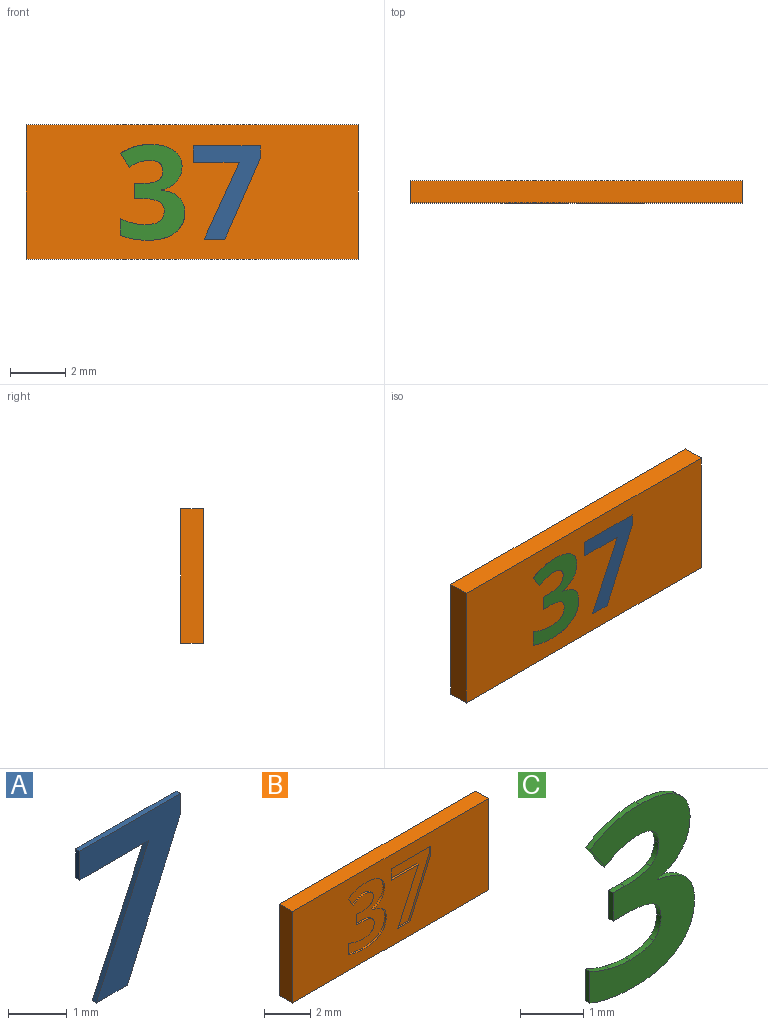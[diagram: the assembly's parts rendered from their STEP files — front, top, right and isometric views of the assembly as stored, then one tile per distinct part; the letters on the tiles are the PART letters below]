
ASSEMBLY  parts=3 mates=2
PART A: 9 faces, bbox 2.4x0.1x3.4 mm
  f0: plane 3.37x2.42mm, normal (0,-1,0), area 3.4mm2, adj f1,f2,f3,f4,f6,f7,f8
  f1: plane 2.92x1.28mm, normal (0.92,0,-0.4), area 0.3mm2, adj f0,f2,f5,f7
  f2: plane 0.45x0.1mm, normal (1,0,0), area 0mm2, adj f0,f1,f3,f5
  f3: plane 2.42x0.1mm, normal (0,0,1), area 0.2mm2, adj f0,f2,f4,f5
  f4: plane 0.6x0.1mm, normal (-1,0,0), area 0.1mm2, adj f0,f3,f5,f6
  f5: plane 3.37x2.42mm, normal (0,1,0), area 3.4mm2, adj f1,f2,f3,f4,f6,f7,f8
  f6: plane 1.66x0.1mm, normal (0,0,-1), area 0.2mm2, adj f0,f4,f5,f8
  f7: plane 0.75x0.1mm, normal (0,0,-1), area 0.1mm2, adj f0,f1,f5,f8
  f8: plane 2.77x1.27mm, normal (-0.91,0,0.42), area 0.3mm2, adj f0,f5,f6,f7
PART B: 42 faces, bbox 12x0.8x4.9 mm
  f0: plane 12x4.85mm, normal (0,-1,0), area 50.5mm2, adj f1,f2,f3,f4,f6,f7,f8,f9
  f1: plane 12x0.8mm, normal (0,0,-1), area 9.6mm2, adj f0,f2,f4,f5
  f2: plane 4.85x0.8mm, normal (1,0,0), area 3.9mm2, adj f0,f1,f3,f5
  f3: plane 12x0.8mm, normal (0,0,1), area 9.6mm2, adj f0,f2,f4,f5
  f4: plane 4.85x0.8mm, normal (-1,0,0), area 3.9mm2, adj f0,f1,f3,f5
  f5: plane 12x4.85mm, normal (0,1,0), area 58.2mm2, adj f1,f2,f3,f4
  f6: plane 0.75x0.1mm, normal (0,0,1), area 0.1mm2, adj f0,f7,f12,f13
  f7: plane 2.92x1.28mm, normal (-0.92,0,0.4), area 0.3mm2, adj f0,f6,f8,f13
  f8: plane 0.45x0.1mm, normal (-1,0,0), area 0mm2, adj f0,f7,f9,f13
  f9: plane 2.42x0.1mm, normal (0,0,-1), area 0.2mm2, adj f0,f8,f10,f13
  f10: plane 0.6x0.1mm, normal (1,0,0), area 0.1mm2, adj f0,f9,f11,f13
  f11: plane 1.66x0.1mm, normal (0,0,1), area 0.2mm2, adj f0,f10,f12,f13
  f12: plane 2.77x1.27mm, normal (0.91,0,-0.42), area 0.3mm2, adj f0,f6,f11,f13
  f13: plane 3.37x2.42mm, normal (0,-1,0), area 3.4mm2, adj f6,f7,f8,f9,f10,f11,f12
  f14: extruded ~0.59x0.3mm, area 0.1mm2, adj f0,f15,f40,f41
  f15: extruded ~0.83x0.21mm, area 0.1mm2, adj f0,f14,f16,f41
  f16: extruded ~1.1x0.33mm, area 0.1mm2, adj f0,f15,f17,f41
  f17: plane 0.49x0.33mm, normal (0.83,0,0.56), area 0.1mm2, adj f0,f16,f18,f41
  f18: extruded ~0.38x0.19mm, area 0mm2, adj f0,f17,f19,f41
  f19: extruded ~0.34x0.1mm, area 0mm2, adj f0,f18,f20,f41
  f20: extruded ~0.48x0.38mm, area 0.1mm2, adj f0,f19,f21,f41
  f21: extruded ~0.35x0.18mm, area 0mm2, adj f0,f20,f22,f41
  f22: extruded ~0.57x0.1mm, area 0.1mm2, adj f0,f21,f23,f41
  f23: plane 0.26x0.1mm, normal (0,0,-1), area 0mm2, adj f0,f22,f24,f41
  f24: plane 0.55x0.1mm, normal (1,0,0), area 0.1mm2, adj f0,f23,f25,f41
  f25: plane 0.26x0.1mm, normal (0,0,1), area 0mm2, adj f0,f24,f26,f41
  f26: extruded ~0.62x0.1mm, area 0.1mm2, adj f0,f25,f27,f41
  f27: extruded ~0.34x0.19mm, area 0mm2, adj f0,f26,f28,f41
  f28: extruded ~0.39x0.17mm, area 0mm2, adj f0,f27,f29,f41
  f29: extruded ~0.52x0.12mm, area 0.1mm2, adj f0,f28,f30,f41
  f30: extruded ~0.47x0.1mm, area 0mm2, adj f0,f29,f31,f41
  f31: extruded ~0.43x0.16mm, area 0mm2, adj f0,f30,f32,f41
  f32: plane 0.61x0.1mm, normal (1,0,0), area 0.1mm2, adj f0,f31,f33,f41
  f33: extruded ~0.97x0.18mm, area 0.1mm2, adj f0,f32,f34,f41
  f34: extruded ~1.01x0.27mm, area 0.1mm2, adj f0,f33,f35,f41
  f35: extruded ~0.76x0.35mm, area 0.1mm2, adj f0,f34,f36,f41
  f36: extruded ~0.53x0.21mm, area 0.1mm2, adj f0,f35,f37,f41
  f37: extruded ~0.62x0.25mm, area 0.1mm2, adj f0,f36,f38,f41
  f38: plane 0.1x0.01mm, normal (-1,0,0), area 0mm2, adj f0,f37,f39,f41
  f39: extruded ~0.54x0.3mm, area 0.1mm2, adj f0,f38,f40,f41
  f40: extruded ~0.54x0.19mm, area 0.1mm2, adj f0,f14,f39,f41
  f41: plane 3.47x2.33mm, normal (0,-1,0), area 4.3mm2, adj f14,f15,f16,f17,f18,f19,f20,f21
PART C: 29 faces, bbox 2.3x0.1x3.5 mm
  f0: plane 3.47x2.33mm, normal (0,-1,0), area 4.3mm2, adj f1,f2,f3,f4,f5,f6,f7,f8
  f1: extruded ~0.83x0.21mm, area 0.1mm2, adj f0,f2,f25,f27
  f2: extruded ~1.1x0.33mm, area 0.1mm2, adj f0,f1,f3,f25
  f3: plane 0.49x0.33mm, normal (-0.83,0,-0.56), area 0.1mm2, adj f0,f2,f4,f25
  f4: extruded ~0.38x0.19mm, area 0mm2, adj f0,f3,f5,f25
  f5: extruded ~0.34x0.1mm, area 0mm2, adj f0,f4,f6,f25
  f6: extruded ~0.48x0.38mm, area 0.1mm2, adj f0,f5,f7,f25
  f7: extruded ~0.35x0.18mm, area 0mm2, adj f0,f6,f8,f25
  f8: extruded ~0.57x0.1mm, area 0.1mm2, adj f0,f7,f9,f25
  f9: plane 0.26x0.1mm, normal (0,0,1), area 0mm2, adj f0,f8,f10,f25
  f10: plane 0.55x0.1mm, normal (-1,0,0), area 0.1mm2, adj f0,f9,f11,f25
  f11: plane 0.26x0.1mm, normal (0,0,-1), area 0mm2, adj f0,f10,f12,f25
  f12: extruded ~0.62x0.1mm, area 0.1mm2, adj f0,f11,f13,f25
  f13: extruded ~0.34x0.19mm, area 0mm2, adj f0,f12,f14,f25
  f14: extruded ~0.39x0.17mm, area 0mm2, adj f0,f13,f15,f25
  f15: extruded ~0.52x0.12mm, area 0.1mm2, adj f0,f14,f16,f25
  f16: extruded ~0.47x0.1mm, area 0mm2, adj f0,f15,f17,f25
  f17: extruded ~0.43x0.16mm, area 0mm2, adj f0,f16,f18,f25
  f18: plane 0.61x0.1mm, normal (-1,0,0), area 0.1mm2, adj f0,f17,f19,f25
  f19: extruded ~0.97x0.18mm, area 0.1mm2, adj f0,f18,f20,f25
  f20: extruded ~1.01x0.27mm, area 0.1mm2, adj f0,f19,f21,f25
  f21: extruded ~0.76x0.35mm, area 0.1mm2, adj f0,f20,f22,f25
  f22: extruded ~0.53x0.21mm, area 0.1mm2, adj f0,f21,f23,f25
  f23: extruded ~0.62x0.25mm, area 0.1mm2, adj f0,f22,f24,f25
  f24: plane 0.1x0.01mm, normal (1,0,0), area 0mm2, adj f0,f23,f25,f26
  f25: plane 3.47x2.33mm, normal (0,1,0), area 4.3mm2, adj f1,f2,f3,f4,f5,f6,f7,f8
  f26: extruded ~0.54x0.3mm, area 0.1mm2, adj f0,f24,f25,f28
  f27: extruded ~0.59x0.3mm, area 0.1mm2, adj f0,f1,f25,f28
  f28: extruded ~0.54x0.19mm, area 0.1mm2, adj f0,f25,f26,f27
PLACE A t=(-0.25,0.38,-0.01)mm
PLACE B t=(-0.03,0.38,-0.01)mm
PLACE C t=(-2.96,0.38,-0.01)mm
MATE fastened C.f0 <-> B.f0  axis (0,-1,0) through (-2.62,-0.42,-1.58)mm
MATE fastened A.f0 <-> B.f0  axis (0,-1,0) through (0.42,-0.42,-1.71)mm
